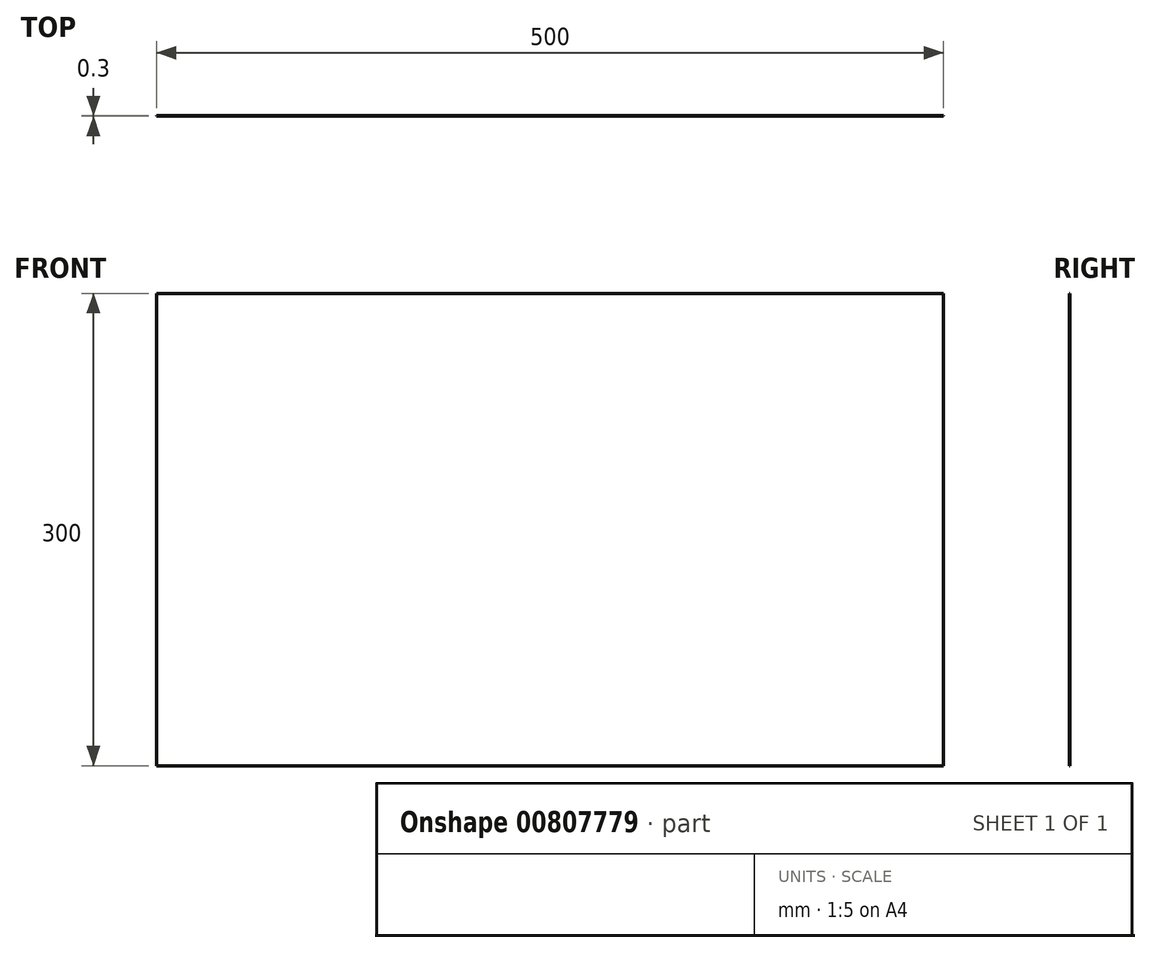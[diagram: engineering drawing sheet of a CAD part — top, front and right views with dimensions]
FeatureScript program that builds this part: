
annotation { "Feature Type Name" : "Feature", "Feature Type Description" : "" }
export const myFeature = defineFeature(function(context is Context, id is Id, definition is map)
    precondition{}
    {
        {
            var Q0;
            Q0=qCreatedBy(makeId("Front.planeOp"),FACE);
            var sketch = newSketch(context, id + "F0", { "sketchPlane" : qUnion([Q0])});
            skLineSegment(sketch, "E0.bottom", {"start": v(0, 0) * mm, "end": v(500, 0) * mm});
            skLineSegment(sketch, "E0.top", {"start": v(0, 300) * mm, "end": v(500, 300) * mm});
            skLineSegment(sketch, "E0.left", {"start": v(0, 0) * mm, "end": v(0, 300) * mm});
            skLineSegment(sketch, "E0.right", {"start": v(500, 0) * mm, "end": v(500, 300) * mm});
            skSolve(sketch);
        }
        {
            var Q0;
            Q0 = qSketchRegion(id + "F0", true);
            extrude(context, id + "F1", {"entities" : qUnion([Q0]), "depth" : .3 * mm, "offsetDistance" : 25 * mm});
        }
    });
